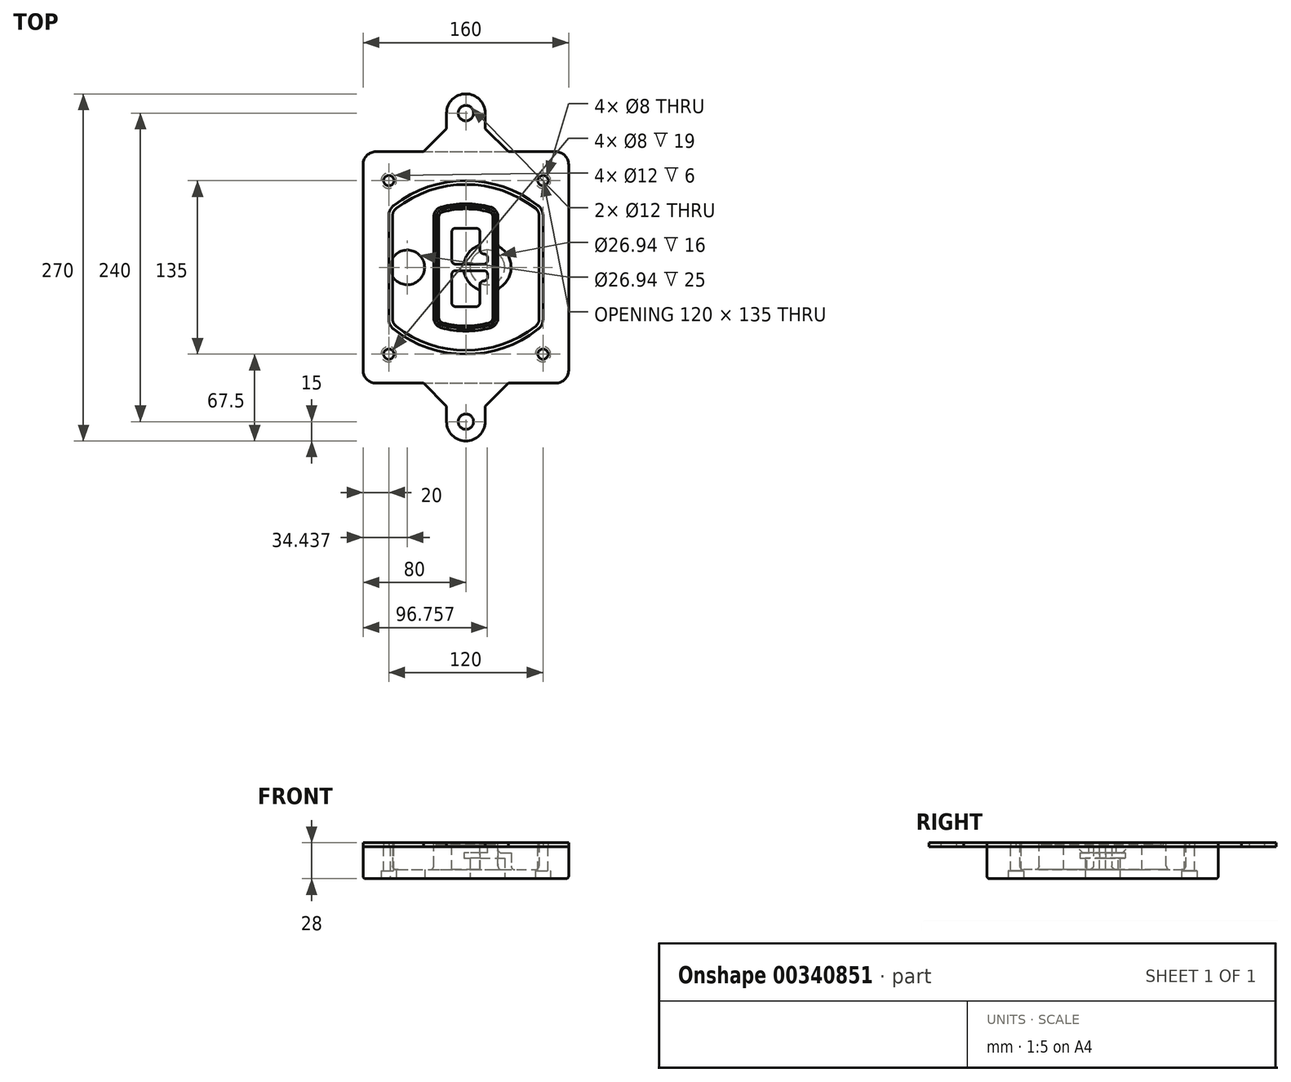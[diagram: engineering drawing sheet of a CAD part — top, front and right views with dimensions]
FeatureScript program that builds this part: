
annotation { "Feature Type Name" : "Feature", "Feature Type Description" : "" }
export const myFeature = defineFeature(function(context is Context, id is Id, definition is map)
    precondition{}
    {
        {
            var Q0;
            Q0=qCreatedBy(makeId("Top.planeOp"),FACE);
            var sketch = newSketch(context, id + "F0", { "sketchPlane" : qUnion([Q0])});
            skPoint(sketch, "E0.rect.middle", {"position": v(0, 0) * mm});
            skLineSegment(sketch, "E1.bottom", {"start": v(-70, -90) * mm, "end": v(70, -90) * mm});
            skLineSegment(sketch, "E1.top", {"start": v(-70, 90) * mm, "end": v(70, 90) * mm});
            skLineSegment(sketch, "E1.left", {"start": v(-80, -80) * mm, "end": v(-80, 80) * mm});
            skLineSegment(sketch, "E1.right", {"start": v(80, -80) * mm, "end": v(80, 80) * mm});
            skLineSegment(sketch, "E2", {"start": v(-80, 90) * mm, "end": v(80, -90) * mm, "construction": true});
            skLineSegment(sketch, "E3", {"start": v(80, 90) * mm, "end": v(-80, -90) * mm, "construction": true});
            skCircle(sketch, "E4", {"center": v(-60, 67.5) * mm, "radius": 4 * mm});
            skCircle(sketch, "E5", {"center": v(60, 67.5) * mm, "radius": 4 * mm});
            skCircle(sketch, "E6", {"center": v(60, -67.5) * mm, "radius": 4 * mm});
            skCircle(sketch, "E7", {"center": v(-60, -67.5) * mm, "radius": 4 * mm});
            skLineSegment(sketch, "E8", {"start": v(-60, 67.5) * mm, "end": v(60, 67.5) * mm, "construction": true});
            skLineSegment(sketch, "E9", {"start": v(60, 67.5) * mm, "end": v(60, -67.5) * mm, "construction": true});
            skLineSegment(sketch, "E10", {"start": v(60, -67.5) * mm, "end": v(-60, -67.5) * mm, "construction": true});
            skLineSegment(sketch, "E11", {"start": v(-60, -67.5) * mm, "end": v(-60, 67.5) * mm, "construction": true});
            skLineSegment(sketch, "E12", {"start": v(-60, 40.3) * mm, "end": v(-60, -40.3) * mm});
            skLineSegment(sketch, "E13", {"start": v(60, 40.3) * mm, "end": v(60, -40.3) * mm});
            skArc(sketch, "E14", {"start": v(56.15, 48.18) * mm, "mid": v(0, 67.5) * mm, "end": v(-56.15, 48.18) * mm});
            skArc(sketch, "E15", {"start": v(-56.15, -48.18) * mm, "mid": v(0, -67.5) * mm, "end": v(56.15, -48.18) * mm});
            skLineSegment(sketch, "E16", {"start": v(-60, 0) * mm, "end": v(60, 0) * mm, "construction": true});
            skPoint(sketch, "E17.visualSharp", {"position": v(-60, -45) * mm});
            skArc(sketch, "E17.filletArc", {"start": v(-60, -40.3) * mm, "mid": v(-58.99, -44.68) * mm, "end": v(-56.15, -48.18) * mm});
            skPoint(sketch, "E18.visualSharp", {"position": v(-60, 45) * mm});
            skArc(sketch, "E18.filletArc", {"start": v(-56.15, 48.18) * mm, "mid": v(-58.99, 44.68) * mm, "end": v(-60, 40.3) * mm});
            skPoint(sketch, "E19.visualSharp", {"position": v(60, 45) * mm});
            skArc(sketch, "E19.filletArc", {"start": v(60, 40.3) * mm, "mid": v(58.99, 44.68) * mm, "end": v(56.15, 48.18) * mm});
            skPoint(sketch, "E20.visualSharp", {"position": v(60, -45) * mm});
            skArc(sketch, "E20.filletArc", {"start": v(56.15, -48.18) * mm, "mid": v(58.99, -44.68) * mm, "end": v(60, -40.3) * mm});
            skPoint(sketch, "E21.visualSharp", {"position": v(-80, 90) * mm});
            skArc(sketch, "E21.filletArc", {"start": v(-70, 90) * mm, "mid": v(-77.07, 87.07) * mm, "end": v(-80, 80) * mm});
            skPoint(sketch, "E22.visualSharp", {"position": v(80, 90) * mm});
            skArc(sketch, "E22.filletArc", {"start": v(80, 80) * mm, "mid": v(77.07, 87.07) * mm, "end": v(70, 90) * mm});
            skPoint(sketch, "E23.visualSharp", {"position": v(80, -90) * mm});
            skArc(sketch, "E23.filletArc", {"start": v(70, -90) * mm, "mid": v(77.07, -87.07) * mm, "end": v(80, -80) * mm});
            skPoint(sketch, "E24.visualSharp", {"position": v(-80, -90) * mm});
            skArc(sketch, "E24.filletArc", {"start": v(-80, -80) * mm, "mid": v(-77.07, -87.07) * mm, "end": v(-70, -90) * mm});
            skArc(sketch, "E25.0", {"start": v(57, 40.3) * mm, "mid": v(56.3, 43.36) * mm, "end": v(54.3, 45.81) * mm});
            skLineSegment(sketch, "E25.1", {"start": v(57, 40.3) * mm, "end": v(57, -40.3) * mm});
            skArc(sketch, "E25.2", {"start": v(54.3, -45.81) * mm, "mid": v(56.3, -43.36) * mm, "end": v(57, -40.3) * mm});
            skArc(sketch, "E25.3", {"start": v(-54.3, -45.81) * mm, "mid": v(0, -64.5) * mm, "end": v(54.3, -45.81) * mm});
            skArc(sketch, "E25.4", {"start": v(-57, -40.3) * mm, "mid": v(-56.3, -43.36) * mm, "end": v(-54.3, -45.81) * mm});
            skArc(sketch, "E25.5", {"start": v(54.3, 45.81) * mm, "mid": v(0, 64.5) * mm, "end": v(-54.3, 45.81) * mm});
            skLineSegment(sketch, "E25.6", {"start": v(-57, 40.3) * mm, "end": v(-57, -40.3) * mm});
            skArc(sketch, "E25.7", {"start": v(-54.3, 45.81) * mm, "mid": v(-56.3, 43.36) * mm, "end": v(-57, 40.3) * mm});
            skArc(sketch, "E26.0", {"start": v(-58.62, 51.33) * mm, "mid": v(-62.58, 46.43) * mm, "end": v(-64, 40.3) * mm});
            skArc(sketch, "E26.1", {"start": v(58.62, 51.33) * mm, "mid": v(0, 71.5) * mm, "end": v(-58.62, 51.33) * mm});
            skArc(sketch, "E26.2", {"start": v(64, 40.3) * mm, "mid": v(62.58, 46.43) * mm, "end": v(58.62, 51.33) * mm});
            skLineSegment(sketch, "E26.3", {"start": v(64, 40.3) * mm, "end": v(64, -40.3) * mm});
            skArc(sketch, "E26.4", {"start": v(58.62, -51.33) * mm, "mid": v(62.58, -46.43) * mm, "end": v(64, -40.3) * mm});
            skLineSegment(sketch, "E26.5", {"start": v(-64, 40.3) * mm, "end": v(-64, -40.3) * mm});
            skArc(sketch, "E26.6", {"start": v(-58.62, -51.33) * mm, "mid": v(0, -71.5) * mm, "end": v(58.62, -51.33) * mm});
            skArc(sketch, "E26.7", {"start": v(-64, -40.3) * mm, "mid": v(-62.58, -46.43) * mm, "end": v(-58.62, -51.33) * mm});
            skSolve(sketch);
        }
        {
            var Q0;
            Q0=makeQuery(id+"F0.imprint","IMPRINT",FACE,{"disambiguationData":[TD([[makeQuery(id+"F0.imprint","IMPRINT",EDGE,{"derivedFrom":sQuery(id+"F0.wireOp",EDGE,"E1.bottom")}),1.0]])]});
            var Q1;
            Q1=makeQuery(id+"F0.imprint","IMPRINT",FACE,{"disambiguationData":[TD([[makeQuery(id+"F0.imprint","IMPRINT",EDGE,{"derivedFrom":sQuery(id+"F0.wireOp",EDGE,"E12")}),1.0]])]});
            var Q2;
            Q2=makeQuery(id+"F0.imprint","IMPRINT",FACE,{"disambiguationData":[TD([[makeQuery(id+"F0.imprint","IMPRINT",EDGE,{"derivedFrom":sQuery(id+"F0.wireOp",EDGE,"E25.0")}),1.0]])]});
            var Q3;
            Q3=makeQuery(id+"F0.imprint","IMPRINT",FACE,{"disambiguationData":[TD([[makeQuery(id+"F0.imprint","IMPRINT",EDGE,{"derivedFrom":sQuery(id+"F0.wireOp",EDGE,"E12")}),-1.0]])]});
            extrude(context, id + "F1", {"entities" : qUnion([Q0, Q1, Q2, Q3]), "oppositeDirection" : true, "depth" : 25 * mm});
        }
        {
            var Q0;
            Q0=makeQuery(id+"F0.imprint","IMPRINT",FACE,{"disambiguationData":[TD([[makeQuery(id+"F0.imprint","IMPRINT",EDGE,{"derivedFrom":sQuery(id+"F0.wireOp",EDGE,"E12")}),1.0]])]});
            extrude(context, id + "F2", {"entities" : qUnion([Q0]), "operationType" : NewBodyOperationType.ADD, "depth" : 3 * mm});
        }
        {
            var Q0;
            Q0=makeQuery(id+"F0.imprint","IMPRINT",FACE,{"disambiguationData":[TD([[makeQuery(id+"F0.imprint","IMPRINT",EDGE,{"derivedFrom":sQuery(id+"F0.wireOp",EDGE,"E25.0")}),1.0]])]});
            extrude(context, id + "F3", {"entities" : qUnion([Q0]), "operationType" : NewBodyOperationType.REMOVE, "oppositeDirection" : true, "depth" : 18 * mm});
        }
        {
            var Q0;
            Q0=makeQuery(id+"F2.opExtrude","CAP_FACE",FACE,{"disambiguationData":[OSD([sQuery(id+"F0.wireOp",EDGE,"E12"),sQuery(id+"F0.wireOp",EDGE,"E13"),sQuery(id+"F0.wireOp",EDGE,"E14"),sQuery(id+"F0.wireOp",EDGE,"E15"),sQuery(id+"F0.wireOp",EDGE,"E17.filletArc"),sQuery(id+"F0.wireOp",EDGE,"E18.filletArc"),sQuery(id+"F0.wireOp",EDGE,"E19.filletArc"),sQuery(id+"F0.wireOp",EDGE,"E20.filletArc"),sQuery(id+"F0.wireOp",EDGE,"E25.0"),sQuery(id+"F0.wireOp",EDGE,"E25.1"),sQuery(id+"F0.wireOp",EDGE,"E25.2"),sQuery(id+"F0.wireOp",EDGE,"E25.3"),sQuery(id+"F0.wireOp",EDGE,"E25.4"),sQuery(id+"F0.wireOp",EDGE,"E25.5"),sQuery(id+"F0.wireOp",EDGE,"E25.6"),sQuery(id+"F0.wireOp",EDGE,"E25.7")])],"isStart":false});
            var sketch = newSketch(context, id + "F4", { "sketchPlane" : qUnion([Q0])});
            skArc(sketch, "E27.0", {"start": v(-19.08, -46.97) * mm, "mid": v(0, -49.5) * mm, "end": v(19.08, -46.97) * mm});
            skArc(sketch, "E28.0", {"start": v(19.08, 46.97) * mm, "mid": v(0, 49.5) * mm, "end": v(-19.08, 46.97) * mm});
            skLineSegment(sketch, "E29", {"start": v(-25, 39.25) * mm, "end": v(-25, -39.25) * mm});
            skLineSegment(sketch, "E30", {"start": v(25, 39.25) * mm, "end": v(25, -39.25) * mm});
            skLineSegment(sketch, "E31", {"start": v(-25, 45.1) * mm, "end": v(25, 45.1) * mm, "construction": true});
            skLineSegment(sketch, "E32", {"start": v(-25, -45.1) * mm, "end": v(25, -45.1) * mm, "construction": true});
            skPoint(sketch, "E33.visualSharp", {"position": v(-25, 45.1) * mm});
            skArc(sketch, "E33.filletArc", {"start": v(-19.08, 46.97) * mm, "mid": v(-23.35, 44.11) * mm, "end": v(-25, 39.25) * mm});
            skPoint(sketch, "E34.visualSharp", {"position": v(25, 45.1) * mm});
            skArc(sketch, "E34.filletArc", {"start": v(25, 39.25) * mm, "mid": v(23.35, 44.11) * mm, "end": v(19.08, 46.97) * mm});
            skPoint(sketch, "E35.visualSharp", {"position": v(25, -45.1) * mm});
            skArc(sketch, "E35.filletArc", {"start": v(19.08, -46.97) * mm, "mid": v(23.35, -44.11) * mm, "end": v(25, -39.25) * mm});
            skPoint(sketch, "E36.visualSharp", {"position": v(-25, -45.1) * mm});
            skArc(sketch, "E36.filletArc", {"start": v(-25, -39.25) * mm, "mid": v(-23.35, -44.11) * mm, "end": v(-19.08, -46.97) * mm});
            skArc(sketch, "E37.0", {"start": v(54.3, 45.81) * mm, "mid": v(0, 64.5) * mm, "end": v(-54.3, 45.81) * mm});
            skArc(sketch, "E37.1", {"start": v(-54.3, 45.81) * mm, "mid": v(-56.3, 43.36) * mm, "end": v(-57, 40.3) * mm});
            skLineSegment(sketch, "E37.2", {"start": v(-57, 40.3) * mm, "end": v(-57, -40.3) * mm});
            skArc(sketch, "E37.3", {"start": v(-57, -40.3) * mm, "mid": v(-56.3, -43.36) * mm, "end": v(-54.3, -45.81) * mm});
            skArc(sketch, "E37.4", {"start": v(-54.3, -45.81) * mm, "mid": v(0, -64.5) * mm, "end": v(54.3, -45.81) * mm});
            skArc(sketch, "E37.5", {"start": v(54.3, -45.81) * mm, "mid": v(56.3, -43.36) * mm, "end": v(57, -40.3) * mm});
            skLineSegment(sketch, "E37.6", {"start": v(57, 40.3) * mm, "end": v(57, -40.3) * mm});
            skArc(sketch, "E37.7", {"start": v(57, 40.3) * mm, "mid": v(56.3, 43.36) * mm, "end": v(54.3, 45.81) * mm});
            skLineSegment(sketch, "E38.0", {"start": v(23, 39.25) * mm, "end": v(23, -39.25) * mm});
            skArc(sketch, "E38.1", {"start": v(18.56, -45.04) * mm, "mid": v(21.76, -42.9) * mm, "end": v(23, -39.25) * mm});
            skArc(sketch, "E38.2", {"start": v(-18.56, -45.04) * mm, "mid": v(0, -47.5) * mm, "end": v(18.56, -45.04) * mm});
            skArc(sketch, "E38.3", {"start": v(-23, -39.25) * mm, "mid": v(-21.76, -42.9) * mm, "end": v(-18.56, -45.04) * mm});
            skLineSegment(sketch, "E38.4", {"start": v(-23, 39.25) * mm, "end": v(-23, -39.25) * mm});
            skArc(sketch, "E38.5", {"start": v(23, 39.25) * mm, "mid": v(21.76, 42.9) * mm, "end": v(18.56, 45.04) * mm});
            skArc(sketch, "E38.6", {"start": v(-18.56, 45.04) * mm, "mid": v(-21.76, 42.9) * mm, "end": v(-23, 39.25) * mm});
            skArc(sketch, "E38.7", {"start": v(18.56, 45.04) * mm, "mid": v(0, 47.5) * mm, "end": v(-18.56, 45.04) * mm});
            skArc(sketch, "E39.0", {"start": v(21, 39.25) * mm, "mid": v(20.18, 41.68) * mm, "end": v(18.04, 43.1) * mm});
            skLineSegment(sketch, "E39.1", {"start": v(21, 39.25) * mm, "end": v(21, -39.25) * mm});
            skArc(sketch, "E39.2", {"start": v(18.04, -43.1) * mm, "mid": v(20.18, -41.68) * mm, "end": v(21, -39.25) * mm});
            skArc(sketch, "E39.3", {"start": v(-18.04, -43.1) * mm, "mid": v(0, -45.5) * mm, "end": v(18.04, -43.1) * mm});
            skArc(sketch, "E39.4", {"start": v(-21, -39.25) * mm, "mid": v(-20.18, -41.68) * mm, "end": v(-18.04, -43.1) * mm});
            skArc(sketch, "E39.5", {"start": v(18.04, 43.1) * mm, "mid": v(0, 45.5) * mm, "end": v(-18.04, 43.1) * mm});
            skLineSegment(sketch, "E39.6", {"start": v(-21, 39.25) * mm, "end": v(-21, -39.25) * mm});
            skArc(sketch, "E39.7", {"start": v(-18.04, 43.1) * mm, "mid": v(-20.18, 41.68) * mm, "end": v(-21, 39.25) * mm});
            skLineSegment(sketch, "E40", {"start": v(-25, 0) * mm, "end": v(25, 0) * mm, "construction": true});
            skLineSegment(sketch, "E41", {"start": v(-11, 5.5) * mm, "end": v(-11, 27.5) * mm});
            skLineSegment(sketch, "E42", {"start": v(-8, 30.5) * mm, "end": v(8, 30.5) * mm});
            skLineSegment(sketch, "E43", {"start": v(11, 27.5) * mm, "end": v(11, 13.5) * mm});
            skLineSegment(sketch, "E44", {"start": v(14, 10.5) * mm, "end": v(14, 10.5) * mm});
            skLineSegment(sketch, "E45", {"start": v(17, 7.5) * mm, "end": v(17, 5.5) * mm});
            skLineSegment(sketch, "E46", {"start": v(14, 2.5) * mm, "end": v(-8, 2.5) * mm});
            skPoint(sketch, "E47.visualSharp", {"position": v(-11, 30.5) * mm});
            skArc(sketch, "E47.filletArc", {"start": v(-8, 30.5) * mm, "mid": v(-10.12, 29.62) * mm, "end": v(-11, 27.5) * mm});
            skPoint(sketch, "E48.visualSharp", {"position": v(11, 30.5) * mm});
            skArc(sketch, "E48.filletArc", {"start": v(11, 27.5) * mm, "mid": v(10.12, 29.62) * mm, "end": v(8, 30.5) * mm});
            skPoint(sketch, "E49.visualSharp", {"position": v(11, 10.5) * mm});
            skArc(sketch, "E49.filletArc", {"start": v(11, 13.5) * mm, "mid": v(11.88, 11.38) * mm, "end": v(14, 10.5) * mm});
            skPoint(sketch, "E50.visualSharp", {"position": v(17, 10.5) * mm});
            skArc(sketch, "E50.filletArc", {"start": v(17, 7.5) * mm, "mid": v(16.12, 9.62) * mm, "end": v(14, 10.5) * mm});
            skPoint(sketch, "E51.visualSharp", {"position": v(17, 2.5) * mm});
            skArc(sketch, "E51.filletArc", {"start": v(14, 2.5) * mm, "mid": v(16.12, 3.38) * mm, "end": v(17, 5.5) * mm});
            skPoint(sketch, "E52.visualSharp", {"position": v(-11, 2.5) * mm});
            skArc(sketch, "E52.filletArc", {"start": v(-11, 5.5) * mm, "mid": v(-10.12, 3.38) * mm, "end": v(-8, 2.5) * mm});
            skLineSegment(sketch, "E53.0.MirrorCS", {"start": v(14, -2.5) * mm, "end": v(-8, -2.5) * mm});
            skArc(sketch, "E54.0.MirrorCS", {"start": v(-11, -5.5) * mm, "mid": v(-10.12, -3.38) * mm, "end": v(-8, -2.5) * mm});
            skLineSegment(sketch, "E55.0.MirrorCS", {"start": v(-11, -5.5) * mm, "end": v(-11, -27.5) * mm});
            skArc(sketch, "E56.0.MirrorCS", {"start": v(-8, -30.5) * mm, "mid": v(-10.12, -29.62) * mm, "end": v(-11, -27.5) * mm});
            skLineSegment(sketch, "E57.0.MirrorCS", {"start": v(-8, -30.5) * mm, "end": v(8, -30.5) * mm});
            skArc(sketch, "E58.0.MirrorCS", {"start": v(11, -27.5) * mm, "mid": v(10.12, -29.62) * mm, "end": v(8, -30.5) * mm});
            skLineSegment(sketch, "E59.0.MirrorCS", {"start": v(11, -27.5) * mm, "end": v(11, -13.5) * mm});
            skArc(sketch, "E60.0.MirrorCS", {"start": v(11, -13.5) * mm, "mid": v(11.88, -11.38) * mm, "end": v(14, -10.5) * mm});
            skArc(sketch, "E61.0.MirrorCS", {"start": v(17, -7.5) * mm, "mid": v(16.12, -9.62) * mm, "end": v(14, -10.5) * mm});
            skLineSegment(sketch, "E62.0.MirrorCS", {"start": v(17, -7.5) * mm, "end": v(17, -5.5) * mm});
            skArc(sketch, "E63.0.MirrorCS", {"start": v(14, -2.5) * mm, "mid": v(16.12, -3.38) * mm, "end": v(17, -5.5) * mm});
            skSolve(sketch);
        }
        {
            var Q0;
            Q0=makeQuery(id+"F4.imprint","IMPRINT",FACE,{"disambiguationData":[TD([[makeQuery(id+"F4.imprint","IMPRINT",EDGE,{"derivedFrom":sQuery(id+"F4.wireOp",EDGE,"E27.0")}),1.0]])]});
            var Q1;
            Q1=makeQuery(id+"F4.imprint","IMPRINT",FACE,{"disambiguationData":[TD([[makeQuery(id+"F4.imprint","IMPRINT",EDGE,{"derivedFrom":sQuery(id+"F4.wireOp",EDGE,"E38.0")}),-1.0]])]});
            var Q2;
            Q2=makeQuery(id+"F4.imprint","IMPRINT",FACE,{"disambiguationData":[TD([[makeQuery(id+"F4.imprint","IMPRINT",EDGE,{"derivedFrom":sQuery(id+"F4.wireOp",EDGE,"E39.0")}),1.0]])]});
            extrude(context, id + "F5", {"entities" : qUnion([Q0, Q1, Q2]), "operationType" : NewBodyOperationType.ADD, "endBound" : BoundingType.UP_TO_NEXT, "oppositeDirection" : true, "depth" : 25 * mm});
        }
        {
            var Q0;
            Q0=makeQuery(id+"F4.imprint","IMPRINT",FACE,{"disambiguationData":[TD([[makeQuery(id+"F4.imprint","IMPRINT",EDGE,{"derivedFrom":sQuery(id+"F4.wireOp",EDGE,"E38.0")}),-1.0]])]});
            extrude(context, id + "F6", {"entities" : qUnion([Q0]), "operationType" : NewBodyOperationType.REMOVE, "oppositeDirection" : true, "depth" : 2 * mm});
        }
        {
            var Q0;
            Q0=makeQuery(id+"F1.opExtrude","CAP_FACE",FACE,{"disambiguationData":[OSD([sQuery(id+"F0.wireOp",EDGE,"E1.bottom"),sQuery(id+"F0.wireOp",EDGE,"E1.top"),sQuery(id+"F0.wireOp",EDGE,"E1.left"),sQuery(id+"F0.wireOp",EDGE,"E1.right"),sQuery(id+"F0.wireOp",EDGE,"E4"),sQuery(id+"F0.wireOp",EDGE,"E5"),sQuery(id+"F0.wireOp",EDGE,"E6"),sQuery(id+"F0.wireOp",EDGE,"E7"),sQuery(id+"F0.wireOp",EDGE,"E21.filletArc"),sQuery(id+"F0.wireOp",EDGE,"E22.filletArc"),sQuery(id+"F0.wireOp",EDGE,"E23.filletArc"),sQuery(id+"F0.wireOp",EDGE,"E24.filletArc")])],"isStart":false});
            var sketch = newSketch(context, id + "F7", { "sketchPlane" : qUnion([Q0])});
            skCircle(sketch, "E64", {"center": v(16.76, 0) * mm, "radius": 13.47 * mm});
            skCircle(sketch, "E65", {"center": v(-45.56, 0) * mm, "radius": 13.47 * mm});
            skLineSegment(sketch, "E66", {"start": v(80, 0) * mm, "end": v(-80, 0) * mm});
            skCircle(sketch, "E67", {"center": v(16.76, 0) * mm, "radius": 18.47 * mm});
            skCircle(sketch, "E68", {"center": v(60, -67.5) * mm, "radius": 6 * mm});
            skCircle(sketch, "E69", {"center": v(-60, -67.5) * mm, "radius": 6 * mm});
            skCircle(sketch, "E70", {"center": v(-60, 67.5) * mm, "radius": 6 * mm});
            skCircle(sketch, "E71", {"center": v(60, 67.5) * mm, "radius": 6 * mm});
            skSolve(sketch);
        }
        {
            var Q0;
            {var subQ1=sQuery(id+"F7.wireOp",EDGE,"E66");var subQ4=sQuery(id+"F7.wireOp",EDGE,"E64");var subQ6=makeQuery(id+"F7.imprint","INTERSECT",VERTEX,{"disambiguationData":[OD(0.0)],"derivedFrom":[subQ4,subQ1]});Q0=makeQuery(id+"F7.imprint","IMPRINT",FACE,{"disambiguationData":[TD([[makeQuery(id+"F7.imprint","IMPRINT",EDGE,{"disambiguationData":[TD([[subQ6,-1.0]])],"derivedFrom":subQ4}),-1.0]])]});}
            var Q1;
            {var subQ0=sQuery(id+"F7.wireOp",EDGE,"E66");var subQ1=sQuery(id+"F7.wireOp",EDGE,"E64");var subQ3=makeQuery(id+"F7.imprint","INTERSECT",VERTEX,{"disambiguationData":[OD(0.0)],"derivedFrom":[subQ1,subQ0]});Q1=makeQuery(id+"F7.imprint","IMPRINT",FACE,{"disambiguationData":[TD([[makeQuery(id+"F7.imprint","IMPRINT",EDGE,{"disambiguationData":[TD([[subQ3,-1.0]])],"derivedFrom":subQ1}),1.0]])]});}
            var Q2;
            {var subQ0=sQuery(id+"F7.wireOp",EDGE,"E66");var subQ1=sQuery(id+"F7.wireOp",EDGE,"E64");var subQ3=makeQuery(id+"F7.imprint","INTERSECT",VERTEX,{"disambiguationData":[OD(0.0)],"derivedFrom":[subQ1,subQ0]});Q2=makeQuery(id+"F7.imprint","IMPRINT",FACE,{"disambiguationData":[TD([[makeQuery(id+"F7.imprint","IMPRINT",EDGE,{"disambiguationData":[TD([[subQ3,1.0]])],"derivedFrom":subQ1}),1.0]])]});}
            var Q3;
            {var subQ1=sQuery(id+"F7.wireOp",EDGE,"E66");var subQ4=sQuery(id+"F7.wireOp",EDGE,"E64");var subQ6=makeQuery(id+"F7.imprint","INTERSECT",VERTEX,{"disambiguationData":[OD(0.0)],"derivedFrom":[subQ4,subQ1]});Q3=makeQuery(id+"F7.imprint","IMPRINT",FACE,{"disambiguationData":[TD([[makeQuery(id+"F7.imprint","IMPRINT",EDGE,{"disambiguationData":[TD([[subQ6,1.0]])],"derivedFrom":subQ4}),-1.0]])]});}
            extrude(context, id + "F8", {"entities" : qUnion([Q0, Q1, Q2, Q3]), "operationType" : NewBodyOperationType.ADD, "oppositeDirection" : true, "depth" : 20 * mm});
        }
        {
            var Q0;
            {var subQ0=sQuery(id+"F7.wireOp",EDGE,"E66");var subQ1=sQuery(id+"F7.wireOp",EDGE,"E64");var subQ3=makeQuery(id+"F7.imprint","INTERSECT",VERTEX,{"disambiguationData":[OD(0.0)],"derivedFrom":[subQ1,subQ0]});Q0=makeQuery(id+"F7.imprint","IMPRINT",FACE,{"disambiguationData":[TD([[makeQuery(id+"F7.imprint","IMPRINT",EDGE,{"disambiguationData":[TD([[subQ3,-1.0]])],"derivedFrom":subQ1}),1.0]])]});}
            var Q1;
            {var subQ0=sQuery(id+"F7.wireOp",EDGE,"E66");var subQ1=sQuery(id+"F7.wireOp",EDGE,"E64");var subQ3=makeQuery(id+"F7.imprint","INTERSECT",VERTEX,{"disambiguationData":[OD(0.0)],"derivedFrom":[subQ1,subQ0]});Q1=makeQuery(id+"F7.imprint","IMPRINT",FACE,{"disambiguationData":[TD([[makeQuery(id+"F7.imprint","IMPRINT",EDGE,{"disambiguationData":[TD([[subQ3,1.0]])],"derivedFrom":subQ1}),1.0]])]});}
            extrude(context, id + "F9", {"entities" : qUnion([Q0, Q1]), "operationType" : NewBodyOperationType.REMOVE, "oppositeDirection" : true, "depth" : 16 * mm});
        }
        {
            var Q0;
            {var subQ0=sQuery(id+"F7.wireOp",EDGE,"E66");var subQ1=sQuery(id+"F7.wireOp",EDGE,"E65");var subQ3=makeQuery(id+"F7.imprint","INTERSECT",VERTEX,{"disambiguationData":[OD(0.0)],"derivedFrom":[subQ1,subQ0]});Q0=makeQuery(id+"F7.imprint","IMPRINT",FACE,{"disambiguationData":[TD([[makeQuery(id+"F7.imprint","IMPRINT",EDGE,{"disambiguationData":[TD([[subQ3,-1.0]])],"derivedFrom":subQ1}),1.0]])]});}
            var Q1;
            {var subQ0=sQuery(id+"F7.wireOp",EDGE,"E66");var subQ1=sQuery(id+"F7.wireOp",EDGE,"E65");var subQ3=makeQuery(id+"F7.imprint","INTERSECT",VERTEX,{"disambiguationData":[OD(0.0)],"derivedFrom":[subQ1,subQ0]});Q1=makeQuery(id+"F7.imprint","IMPRINT",FACE,{"disambiguationData":[TD([[makeQuery(id+"F7.imprint","IMPRINT",EDGE,{"disambiguationData":[TD([[subQ3,1.0]])],"derivedFrom":subQ1}),1.0]])]});}
            extrude(context, id + "F10", {"entities" : qUnion([Q0, Q1]), "operationType" : NewBodyOperationType.REMOVE, "oppositeDirection" : true, "depth" : 25 * mm});
        }
        {
            var Q0;
            Q0=makeQuery(id+"F7.imprint","IMPRINT",FACE,{"disambiguationData":[TD([[makeQuery(id+"F7.imprint","IMPRINT",EDGE,{"derivedFrom":sQuery(id+"F7.wireOp",EDGE,"E68")}),1.0]])]});
            var Q1;
            Q1=makeQuery(id+"F7.imprint","IMPRINT",FACE,{"disambiguationData":[TD([[makeQuery(id+"F7.imprint","IMPRINT",EDGE,{"derivedFrom":makeQuery(id+"F1.opExtrude","CAP_EDGE",EDGE,{"disambiguationData":[OSD([sQuery(id+"F0.wireOp",EDGE,"E5")])],"isStart":false})}),-1.0]])]});
            var Q2;
            Q2=makeQuery(id+"F7.imprint","IMPRINT",FACE,{"disambiguationData":[TD([[makeQuery(id+"F7.imprint","IMPRINT",EDGE,{"derivedFrom":sQuery(id+"F7.wireOp",EDGE,"E69")}),1.0]])]});
            var Q3;
            Q3=makeQuery(id+"F7.imprint","IMPRINT",FACE,{"disambiguationData":[TD([[makeQuery(id+"F7.imprint","IMPRINT",EDGE,{"derivedFrom":makeQuery(id+"F1.opExtrude","CAP_EDGE",EDGE,{"disambiguationData":[OSD([sQuery(id+"F0.wireOp",EDGE,"E4")])],"isStart":false})}),-1.0]])]});
            var Q4;
            Q4=makeQuery(id+"F7.imprint","IMPRINT",FACE,{"disambiguationData":[TD([[makeQuery(id+"F7.imprint","IMPRINT",EDGE,{"derivedFrom":sQuery(id+"F7.wireOp",EDGE,"E70")}),1.0]])]});
            var Q5;
            Q5=makeQuery(id+"F7.imprint","IMPRINT",FACE,{"disambiguationData":[TD([[makeQuery(id+"F7.imprint","IMPRINT",EDGE,{"derivedFrom":makeQuery(id+"F1.opExtrude","CAP_EDGE",EDGE,{"disambiguationData":[OSD([sQuery(id+"F0.wireOp",EDGE,"E7")])],"isStart":false})}),-1.0]])]});
            var Q6;
            Q6=makeQuery(id+"F7.imprint","IMPRINT",FACE,{"disambiguationData":[TD([[makeQuery(id+"F7.imprint","IMPRINT",EDGE,{"derivedFrom":sQuery(id+"F7.wireOp",EDGE,"E71")}),1.0]])]});
            var Q7;
            Q7=makeQuery(id+"F7.imprint","IMPRINT",FACE,{"disambiguationData":[TD([[makeQuery(id+"F7.imprint","IMPRINT",EDGE,{"derivedFrom":makeQuery(id+"F1.opExtrude","CAP_EDGE",EDGE,{"disambiguationData":[OSD([sQuery(id+"F0.wireOp",EDGE,"E6")])],"isStart":false})}),-1.0]])]});
            extrude(context, id + "F11", {"entities" : qUnion([Q0, Q1, Q2, Q3, Q4, Q5, Q6, Q7]), "operationType" : NewBodyOperationType.REMOVE, "oppositeDirection" : true, "depth" : 6 * mm});
        }
        {
            var Q0;
            Q0=makeQuery(id+"F9.boolean.opBoolean","COPY",FACE,{"derivedFrom":makeQuery(id+"F9.opExtrude","CAP_FACE",FACE,{"disambiguationData":[OSD([sQuery(id+"F7.wireOp",EDGE,"E64")])],"isStart":false})});
            var sketch = newSketch(context, id + "F12", { "sketchPlane" : qUnion([Q0])});
            skArc(sketch, "E72.0", {"start": v(11, 17.55) * mm, "mid": v(2.57, 11.82) * mm, "end": v(-1.54, 2.5) * mm});
            skArc(sketch, "E72.1", {"start": v(-1.54, -2.5) * mm, "mid": v(2.57, -11.82) * mm, "end": v(11, -17.55) * mm});
            skLineSegment(sketch, "E73", {"start": v(-1.54, -2.5) * mm, "end": v(14, -2.5) * mm});
            skLineSegment(sketch, "E74.0", {"start": v(14, 2.5) * mm, "end": v(-1.54, 2.5) * mm});
            skArc(sketch, "E74.1", {"start": v(14, 2.5) * mm, "mid": v(16.12, 3.38) * mm, "end": v(17, 5.5) * mm});
            skLineSegment(sketch, "E74.2", {"start": v(17, 7.5) * mm, "end": v(17, 5.5) * mm});
            skArc(sketch, "E74.3", {"start": v(17, 7.5) * mm, "mid": v(16.12, 9.62) * mm, "end": v(14, 10.5) * mm});
            skArc(sketch, "E74.4", {"start": v(11, 13.5) * mm, "mid": v(11.88, 11.38) * mm, "end": v(14, 10.5) * mm});
            skLineSegment(sketch, "E74.5", {"start": v(11, 17.55) * mm, "end": v(11, 13.5) * mm});
            skLineSegment(sketch, "E74.7", {"start": v(14, -2.5) * mm, "end": v(-1.54, -2.5) * mm});
            skArc(sketch, "E74.8", {"start": v(14, -2.5) * mm, "mid": v(16.12, -3.38) * mm, "end": v(17, -5.5) * mm});
            skLineSegment(sketch, "E74.9", {"start": v(17, -7.5) * mm, "end": v(17, -5.5) * mm});
            skArc(sketch, "E74.10", {"start": v(17, -7.5) * mm, "mid": v(16.12, -9.62) * mm, "end": v(14, -10.5) * mm});
            skArc(sketch, "E74.11", {"start": v(11, -13.5) * mm, "mid": v(11.88, -11.38) * mm, "end": v(14, -10.5) * mm});
            skLineSegment(sketch, "E74.12", {"start": v(11, -17.55) * mm, "end": v(11, -13.5) * mm});
            skPoint(sketch, "E75.orphan", {"position": v(11, -27.5) * mm});
            skPoint(sketch, "E76.orphan", {"position": v(-8, -2.5) * mm});
            skPoint(sketch, "E77.orphan", {"position": v(-8, 2.5) * mm});
            skPoint(sketch, "E78.orphan", {"position": v(11, 27.5) * mm});
            skSolve(sketch);
        }
        {
            var Q0;
            {var subQ7=sQuery(id+"F12.wireOp",EDGE,"E72.0");var subQ14=sQuery(id+"F12.wireOp",EDGE,"E72.1");var subQ16=sQuery(id+"F12.wireOp",EDGE,"E74.1");var subQ18=sQuery(id+"F12.wireOp",EDGE,"E74.8");Q0=qUnion([makeQuery(id+"F12.imprint","IMPRINT",FACE,{"disambiguationData":[TD([[makeQuery(id+"F12.imprint","IMPRINT",EDGE,{"derivedFrom":subQ7}),1.0]])]}),makeQuery(id+"F12.imprint","IMPRINT",FACE,{"disambiguationData":[TD([[makeQuery(id+"F12.imprint","IMPRINT",EDGE,{"derivedFrom":subQ14}),1.0]])]}),makeQuery(id+"F12.imprint","IMPRINT",FACE,{"disambiguationData":[TD([[makeQuery(id+"F12.imprint","IMPRINT",EDGE,{"derivedFrom":subQ16}),1.0]])]}),makeQuery(id+"F12.imprint","IMPRINT",FACE,{"disambiguationData":[TD([[makeQuery(id+"F12.imprint","IMPRINT",EDGE,{"derivedFrom":subQ18}),-1.0]])]})]);}
            var Q1;
            Q1=makeQuery(id+"F5.boolean.opBoolean","SPLIT",FACE,{"disambiguationData":[TD([makeQuery(id+"F5.opExtrude","SWEPT_FACE",FACE,{"disambiguationData":[OSD([sQuery(id+"F4.wireOp",EDGE,"E41")])]})])],"derivedFrom":makeQuery(id+"F3.boolean.opBoolean","COPY",FACE,{"derivedFrom":makeQuery(id+"F3.opExtrude","CAP_FACE",FACE,{"disambiguationData":[OSD([sQuery(id+"F0.wireOp",EDGE,"E25.0"),sQuery(id+"F0.wireOp",EDGE,"E25.1"),sQuery(id+"F0.wireOp",EDGE,"E25.2"),sQuery(id+"F0.wireOp",EDGE,"E25.3"),sQuery(id+"F0.wireOp",EDGE,"E25.4"),sQuery(id+"F0.wireOp",EDGE,"E25.5"),sQuery(id+"F0.wireOp",EDGE,"E25.6"),sQuery(id+"F0.wireOp",EDGE,"E25.7")])],"isStart":false})})});
            extrude(context, id + "F13", {"entities" : qUnion([Q0]), "operationType" : NewBodyOperationType.REMOVE, "endBound" : BoundingType.UP_TO_SURFACE, "endBoundEntityFace" : qUnion([Q1]), "depth" : 25 * mm});
        }
        {
            var Q0;
            Q0=makeQuery(id+"F3.boolean.opBoolean","COPY",EDGE,{"derivedFrom":makeQuery(id+"F3.opExtrude","CAP_EDGE",EDGE,{"disambiguationData":[OSD([sQuery(id+"F0.wireOp",EDGE,"E25.6")])],"isStart":false})});
            var Q1;
            Q1=makeQuery(id+"F8.boolean.opBoolean","INTERSECT",EDGE,{"derivedFrom":[makeQuery(id+"F5.opExtrude","SWEPT_FACE",FACE,{"disambiguationData":[OSD([sQuery(id+"F4.wireOp",EDGE,"E30")])]}),makeQuery(id+"F8.opExtrude","CAP_FACE",FACE,{"disambiguationData":[OSD([sQuery(id+"F7.wireOp",EDGE,"E67")])],"isStart":false})]});
            var Q2;
            Q2=makeQuery(id+"F8.boolean.opBoolean","INTERSECT",EDGE,{"disambiguationData":[OD(1.0)],"derivedFrom":[makeQuery(id+"F5.opExtrude","SWEPT_FACE",FACE,{"disambiguationData":[OSD([sQuery(id+"F4.wireOp",EDGE,"E30")])]}),makeQuery(id+"F8.opExtrude","SWEPT_FACE",FACE,{"disambiguationData":[OSD([sQuery(id+"F7.wireOp",EDGE,"E67")])]})]});
            var Q3;
            {var subQ0=sQuery(id+"F4.wireOp",EDGE,"E30");Q3=makeQuery(id+"F8.boolean.opBoolean","SPLIT",EDGE,{"disambiguationData":[TD([makeQuery(id+"F5.opExtrude","SWEPT_FACE",FACE,{"disambiguationData":[OSD([sQuery(id+"F4.wireOp",EDGE,"E35.filletArc")])]})])],"derivedFrom":makeQuery(id+"F5.opExtrude","CAP_EDGE",EDGE,{"disambiguationData":[OSD([subQ0])],"isStart":false})});}
            var Q4;
            {var subQ0=sQuery(id+"F0.wireOp",EDGE,"E25.7");var subQ1=sQuery(id+"F0.wireOp",EDGE,"E25.1");var subQ2=sQuery(id+"F0.wireOp",EDGE,"E25.6");var subQ3=sQuery(id+"F0.wireOp",EDGE,"E25.5");var subQ4=sQuery(id+"F0.wireOp",EDGE,"E25.4");var subQ5=sQuery(id+"F0.wireOp",EDGE,"E25.0");var subQ6=sQuery(id+"F0.wireOp",EDGE,"E25.2");var subQ7=sQuery(id+"F0.wireOp",EDGE,"E25.3");Q4=makeQuery(id+"F8.boolean.opBoolean","INTERSECT",EDGE,{"derivedFrom":[makeQuery(id+"F5.boolean.opBoolean","SPLIT",FACE,{"disambiguationData":[TD([makeQuery(id+"F2.opExtrude","SWEPT_FACE",FACE,{"disambiguationData":[OSD([subQ5])]})])],"derivedFrom":makeQuery(id+"F3.boolean.opBoolean","COPY",FACE,{"derivedFrom":makeQuery(id+"F3.opExtrude","CAP_FACE",FACE,{"disambiguationData":[OSD([subQ5,subQ1,subQ6,subQ7,subQ4,subQ3,subQ2,subQ0])],"isStart":false})})}),makeQuery(id+"F8.opExtrude","SWEPT_FACE",FACE,{"disambiguationData":[OSD([sQuery(id+"F7.wireOp",EDGE,"E67")])]})]});}
            var Q5;
            Q5=makeQuery(id+"F8.boolean.opBoolean","INTERSECT",EDGE,{"disambiguationData":[OD(0.0)],"derivedFrom":[makeQuery(id+"F5.opExtrude","SWEPT_FACE",FACE,{"disambiguationData":[OSD([sQuery(id+"F4.wireOp",EDGE,"E30")])]}),makeQuery(id+"F8.opExtrude","SWEPT_FACE",FACE,{"disambiguationData":[OSD([sQuery(id+"F7.wireOp",EDGE,"E67")])]})]});
            fillet(context, id + "F14", {"entities" : qUnion([Q0, Q1, Q2, Q3, Q4, Q5]), "radius" : 3 * mm, "tangentPropagation" : true, "allowEdgeOverflow" : false});
        }
        {
            var Q0;
            Q0=makeQuery(id+"F1.opExtrude","CAP_EDGE",EDGE,{"disambiguationData":[OSD([sQuery(id+"F0.wireOp",EDGE,"E1.bottom")])],"isStart":false});
            fillet(context, id + "F15", {"entities" : qUnion([Q0]), "radius" : 2 * mm, "tangentPropagation" : true, "allowEdgeOverflow" : false});
        }
        {
            var Q0;
            {var subQ0=sQuery(id+"F0.wireOp",EDGE,"E21.filletArc");var subQ1=sQuery(id+"F0.wireOp",EDGE,"E7");var subQ2=sQuery(id+"F0.wireOp",EDGE,"E6");var subQ3=sQuery(id+"F0.wireOp",EDGE,"E5");var subQ4=sQuery(id+"F0.wireOp",EDGE,"E4");var subQ5=sQuery(id+"F0.wireOp",EDGE,"E22.filletArc");var subQ6=sQuery(id+"F0.wireOp",EDGE,"E1.bottom");var subQ7=sQuery(id+"F0.wireOp",EDGE,"E1.right");var subQ8=sQuery(id+"F0.wireOp",EDGE,"E1.top");var subQ9=sQuery(id+"F0.wireOp",EDGE,"E1.left");var subQ10=sQuery(id+"F0.wireOp",EDGE,"E23.filletArc");var subQ11=sQuery(id+"F0.wireOp",EDGE,"E24.filletArc");Q0=makeQuery(id+"F2.boolean.opBoolean","SPLIT",FACE,{"disambiguationData":[TD([makeQuery(id+"F1.opExtrude","SWEPT_FACE",FACE,{"disambiguationData":[OSD([subQ6])]})])],"derivedFrom":makeQuery(id+"F1.opExtrude","CAP_FACE",FACE,{"disambiguationData":[OSD([subQ6,subQ8,subQ9,subQ7,subQ4,subQ3,subQ2,subQ1,subQ0,subQ5,subQ10,subQ11])],"isStart":true})});}
            var sketch = newSketch(context, id + "F16", { "sketchPlane" : qUnion([Q0])});
            skLineSegment(sketch, "E79", {"start": v(15, 108) * mm, "end": v(15, 120) * mm});
            skArc(sketch, "E80", {"start": v(15, 120) * mm, "mid": v(0, 135) * mm, "end": v(-15, 120) * mm});
            skCircle(sketch, "E81", {"center": v(0, 120) * mm, "radius": 6 * mm});
            skLineSegment(sketch, "E82", {"start": v(0, 120) * mm, "end": v(0, 90) * mm, "construction": true});
            skLineSegment(sketch, "E83.MirrorCS", {"start": v(-15, 108) * mm, "end": v(-15, 120) * mm});
            skArc(sketch, "E84.MirrorCS", {"start": v(-15, 120) * mm, "mid": v(0, 135) * mm, "end": v(15, 120) * mm});
            skLineSegment(sketch, "E85", {"start": v(-80, 0) * mm, "end": v(80, 0) * mm, "construction": true});
            skLineSegment(sketch, "E86", {"start": v(15, 108) * mm, "end": v(33, 90) * mm});
            skLineSegment(sketch, "E87", {"start": v(-15, 108) * mm, "end": v(-33, 90) * mm});
            skLineSegment(sketch, "E88.MirrorCS", {"start": v(0, -120) * mm, "end": v(0, -90) * mm, "construction": true});
            skLineSegment(sketch, "E89.MirrorCS", {"start": v(15, -108) * mm, "end": v(33, -90) * mm});
            skLineSegment(sketch, "E90.MirrorCS", {"start": v(15, -108) * mm, "end": v(15, -120) * mm});
            skArc(sketch, "E91.MirrorCS", {"start": v(-15, -120) * mm, "mid": v(0, -135) * mm, "end": v(15, -120) * mm});
            skLineSegment(sketch, "E92.MirrorCS", {"start": v(-15, -108) * mm, "end": v(-15, -120) * mm});
            skLineSegment(sketch, "E93.MirrorCS", {"start": v(-15, -108) * mm, "end": v(-33, -90) * mm});
            skCircle(sketch, "E94.MirrorC", {"center": v(0, -120) * mm, "radius": 6 * mm});
            skSolve(sketch);
        }
        {
            var Q0;
            Q0=makeQuery(id+"F16.imprint","IMPRINT",FACE,{"disambiguationData":[TD([[makeQuery(id+"F16.imprint","IMPRINT",EDGE,{"derivedFrom":sQuery(id+"F16.wireOp",EDGE,"E79")}),1.0]])]});
            var Q1;
            Q1=makeQuery(id+"F16.imprint","IMPRINT",FACE,{"disambiguationData":[TD([[makeQuery(id+"F16.imprint","IMPRINT",EDGE,{"derivedFrom":makeQuery(id+"F1.opExtrude","CAP_EDGE",EDGE,{"disambiguationData":[OSD([sQuery(id+"F0.wireOp",EDGE,"E1.left")])],"isStart":true})}),-1.0]])]});
            var Q2;
            {var subQ0=sQuery(id+"F16.wireOp",EDGE,"E89.MirrorCS");Q2=makeQuery(id+"F16.imprint","IMPRINT",FACE,{"disambiguationData":[TD([[makeQuery(id+"F16.imprint","IMPRINT",EDGE,{"derivedFrom":subQ0}),1.0]])]});}
            var Q3;
            Q3=makeQuery(id+"F2.opExtrude","CAP_FACE",FACE,{"disambiguationData":[OSD([sQuery(id+"F0.wireOp",EDGE,"E12"),sQuery(id+"F0.wireOp",EDGE,"E13"),sQuery(id+"F0.wireOp",EDGE,"E14"),sQuery(id+"F0.wireOp",EDGE,"E15"),sQuery(id+"F0.wireOp",EDGE,"E17.filletArc"),sQuery(id+"F0.wireOp",EDGE,"E18.filletArc"),sQuery(id+"F0.wireOp",EDGE,"E19.filletArc"),sQuery(id+"F0.wireOp",EDGE,"E20.filletArc"),sQuery(id+"F0.wireOp",EDGE,"E25.0"),sQuery(id+"F0.wireOp",EDGE,"E25.1"),sQuery(id+"F0.wireOp",EDGE,"E25.2"),sQuery(id+"F0.wireOp",EDGE,"E25.3"),sQuery(id+"F0.wireOp",EDGE,"E25.4"),sQuery(id+"F0.wireOp",EDGE,"E25.5"),sQuery(id+"F0.wireOp",EDGE,"E25.6"),sQuery(id+"F0.wireOp",EDGE,"E25.7")])],"isStart":false});
            extrude(context, id + "F17", {"entities" : qUnion([Q0, Q1, Q2]), "endBound" : BoundingType.UP_TO_SURFACE, "endBoundEntityFace" : qUnion([Q3]), "depth" : 25 * mm});
        }
    });
